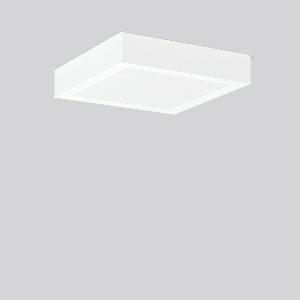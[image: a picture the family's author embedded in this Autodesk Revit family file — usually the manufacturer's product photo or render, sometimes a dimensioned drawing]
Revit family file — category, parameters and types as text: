
# Revit family: toledo_flat_square_a_672277_002_1ffd
name_source: partatom
category: Lighting Fixtures
units: mm (PartAtom-declared; Revit-internal decimal feet)

## family parameters
Cut with Voids When Loaded = No
Host = Face
Light Source = No
Part Type = Normal
Room Calculation Point = No
Round Connector Dimension = Use Diameter
Shared = No

## types (1)
- TOLEDO FLAT square A (1 x LED Modul 830, 2050 lm, 3000)
    Apparent Load = 25 VA
    CIE Flux Codes = 48 80 96 100 100
    Color Rendering = 80
    Color Temperature = 3000
    Default Elevation = 1800 mm
    Description = Series: TOLEDO FLAT square
Ultra thin surface mounted downlight. For escape route illumination. Surface mounted housing: sheet steel, powder-coated. Square cover plate: die-cast aluminium, powder coated. Light guide and diffuser made of non-yellowing PMMA, opal matt. Betriebsgeräte integriert. Einzelbatteriesystem mit automatischem Selbsttest. 
Colour: white
Length: 300 mm
Width: 300 mm
Height: 58 mm
Weight: 3.95 kg
Operating mode: maintained power mode
Duration time: 3 h
Lamp: LED
Socket: without socket
Colour temperature: 3000K
Colour rendering index (CRI): 80
System power: 25 W
Rated luminous flux: 2050 lm
Luminous flux, emergency: 420 lm
System power, emergency: -
Control gear: Regulated power supply
Protection class: I
Type of protection: IP 40
    Height = 58 mm
    Lamp = 1 x LED Modul 830
    Lamp Light Flux = 2050 lm
    Lamp count = 1
    Length = 300 mm
    Lifetime = 50000 h
    Luminous efficacy = 82 lm/W
    Manufacturer = RZB
    ModVariant = No
    Model = 672277.002
    Mounting Place = Ceiling
    Mounting Type = Surface mounted
    Number of Poles = 1
    OnlyDefault = Yes
    Power Factor = 1
    Product Name = TOLEDO FLAT square A
    Product group = Surface mounted downlights
    ProductGroupID = 302
    Protection Class = Protection class I
    Protection Degree = IP 40
    RLX_Detail_Level = 1
    RLX_Emergency_Light_Flux = 420 lm
    RLX_Emergency_Type = 3
    RLX_Emergency_Type_DB = Yes
    RlxData = <blob elided: 13941 chars, md5=beaf983b>
    Socket = socket
    Standby Power = 0 W
    System Light Flux = 2050 lm
    System Power = 25 W
    Type Comments = Product without accessories
    Type Image = 901554.002.jpg
    URL = http://relux.com
    VarID = ---
    Voltage = 0 V
    Weight = 0.00 kg
    Width = 300 mm

## geometry (parser evidence)
native form markers: Sweep x11
no freeform markers — native parametric forms only
